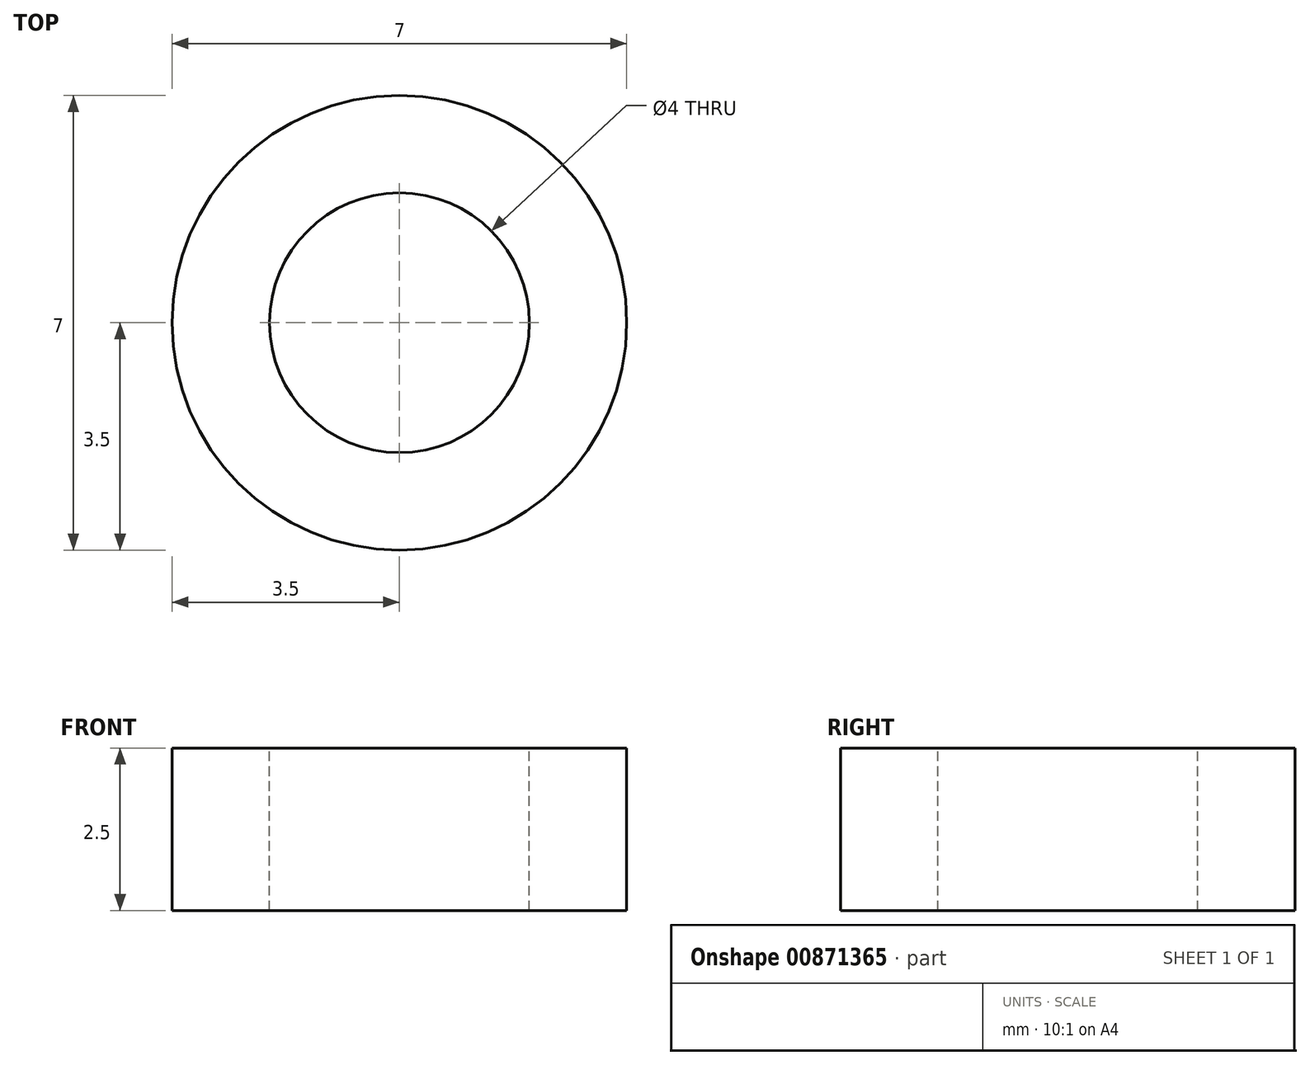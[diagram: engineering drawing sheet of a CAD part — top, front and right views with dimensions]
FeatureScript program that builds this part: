
annotation { "Feature Type Name" : "Feature", "Feature Type Description" : "" }
export const myFeature = defineFeature(function(context is Context, id is Id, definition is map)
    precondition{}
    {
        {
            var Q0;
            Q0=qCreatedBy(makeId("Top.planeOp"),FACE);
            var sketch = newSketch(context, id + "F0", { "sketchPlane" : qUnion([Q0])});
            skCircle(sketch, "E0", {"center": v(0, 0) * mm, "radius": 3.5 * mm});
            skSolve(sketch);
        }
        {
            var Q0;
            Q0=qSketchRegion(id+"F0",true);
            extrude(context, id + "F1", {"entities" : qUnion([Q0]), "depth" : 2.5 * mm, "offsetDistance" : 25 * mm});
        }
        {
            var Q0;
            Q0=makeQuery(id+"F1.opExtrude","CAP_FACE",FACE,{"disambiguationData":[OSD([sQuery(id+"F0.wireOp",EDGE,"E0")])],"isStart":false});
            var sketch = newSketch(context, id + "F2", { "sketchPlane" : qUnion([Q0])});
            skCircle(sketch, "E1", {"center": v(0, 0) * mm, "radius": 2 * mm});
            skSolve(sketch);
        }
        {
            var Q0;
            Q0=qSketchRegion(id+"F2",true);
            extrude(context, id + "F3", {"entities" : qUnion([Q0]), "operationType" : NewBodyOperationType.REMOVE, "endBound" : BoundingType.THROUGH_ALL, "oppositeDirection" : true, "depth" : 25 * mm, "offsetDistance" : 25 * mm});
        }
    });
